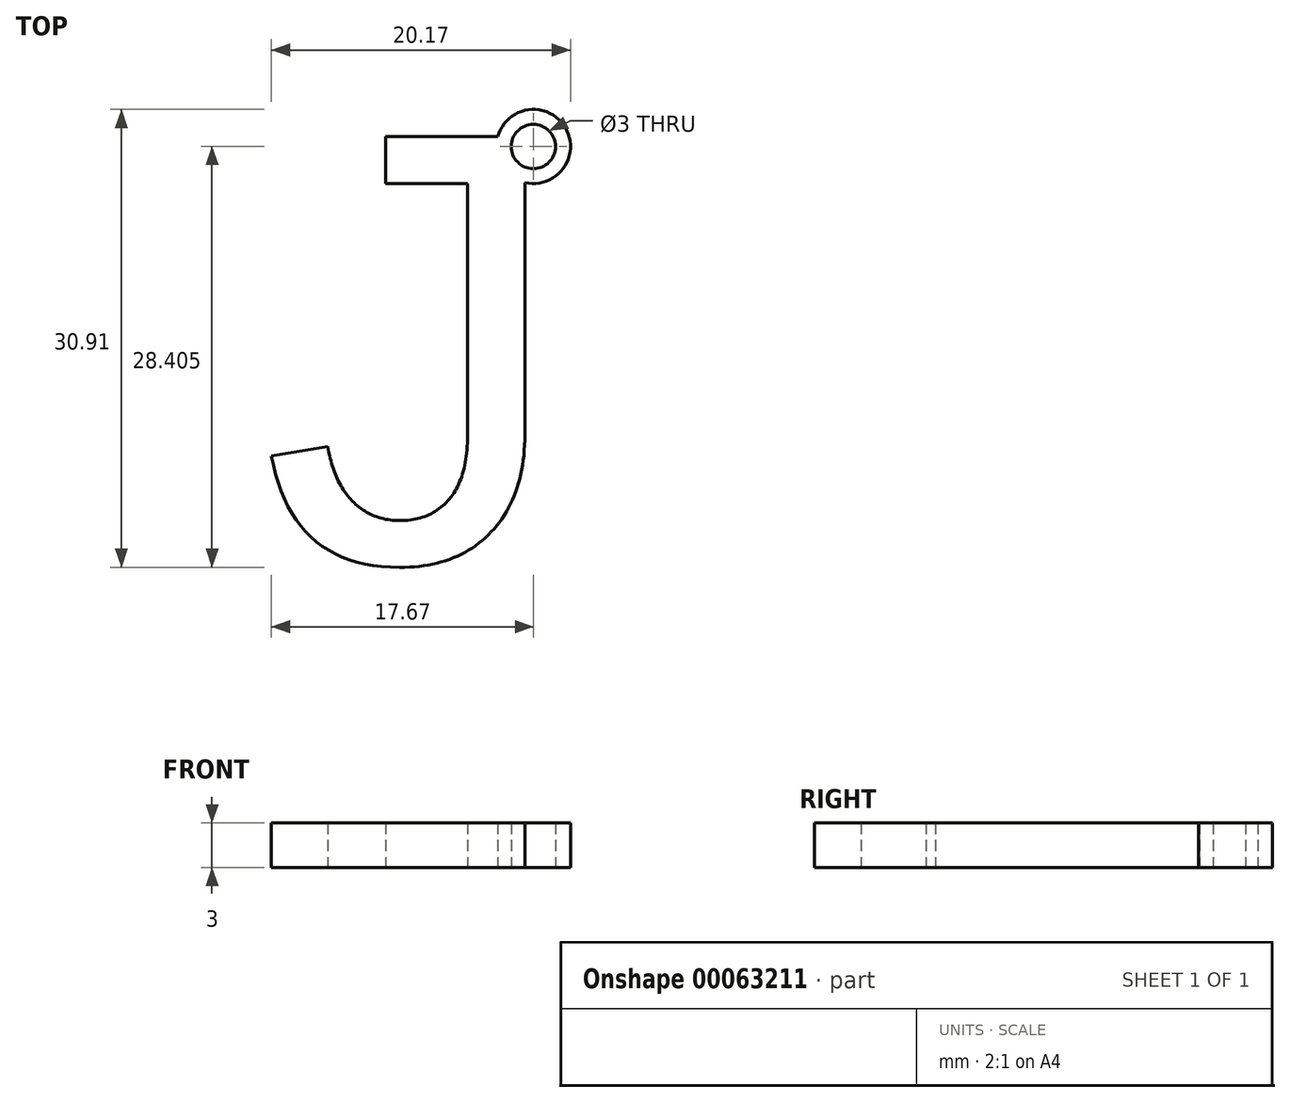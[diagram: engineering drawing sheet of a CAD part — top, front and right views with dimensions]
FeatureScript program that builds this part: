
annotation { "Feature Type Name" : "Feature", "Feature Type Description" : "" }
export const myFeature = defineFeature(function(context is Context, id is Id, definition is map)
    precondition{}
    {
        {
            var Q0;
            Q0=qCreatedBy(makeId("Top.planeOp"),FACE);
            var sketch = newSketch(context, id + "F0", { "sketchPlane" : qUnion([Q0])});
            skText(sketch, "E0", { "text": "J", "fontName": "Arimo-Regular.ttf"});
            skCircle(sketch, "E1", {"center": v(-49.33, 5.05) * mm, "radius": 1.5 * mm});
            skCircle(sketch, "E2", {"center": v(-49.33, 5.05) * mm, "radius": 2.5 * mm});
            const initialGuessF0  = {"E0": [-0.06765, -0.02295, 1, 0, 0.03]};
            skSetInitialGuess(sketch, initialGuessF0);
            skSolve(sketch);
        }
        {
            var Q0;
            Q0 = qSketchRegion(id + "F0", true);
            extrude(context, id + "F1", {"entities" : qUnion([Q0]), "depth" : 3 * mm});
        }
    });
